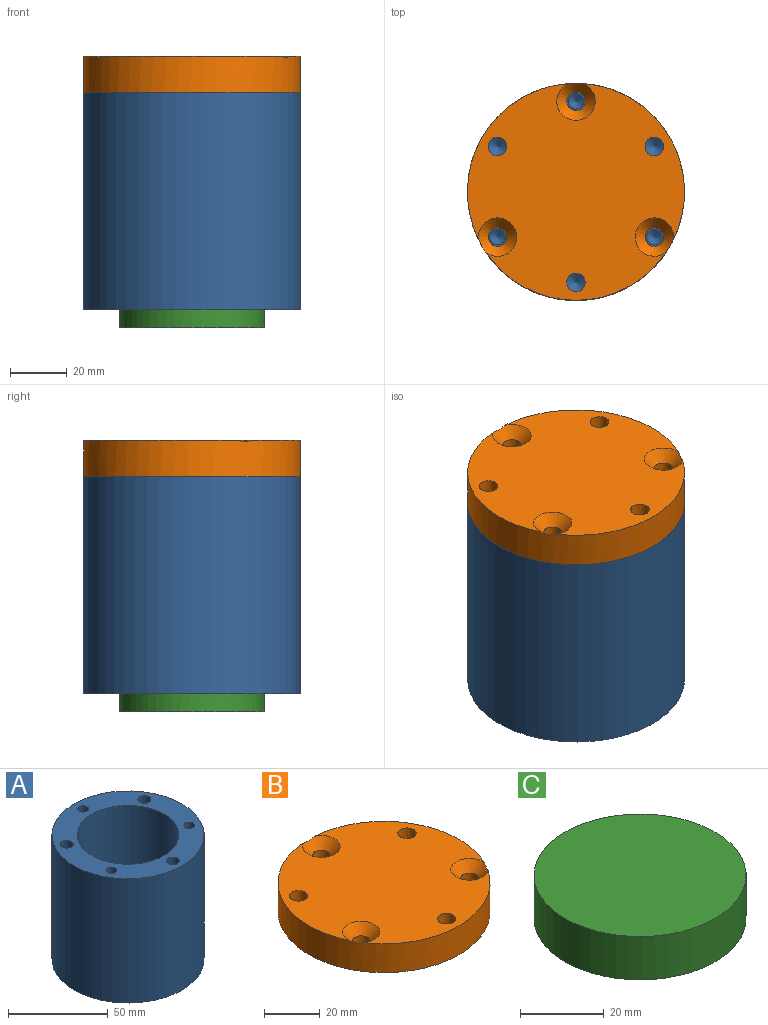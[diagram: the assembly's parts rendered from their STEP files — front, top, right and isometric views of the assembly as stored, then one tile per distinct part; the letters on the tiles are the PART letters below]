
ASSEMBLY  parts=3 mates=3
PART A: 16 faces, bbox 76.2x76.2x76.2 mm
  f0: cylinder r=25.5mm len=76.2mm, axis (0,0,-1), area 12208.9mm2, adj f2,f3
  f1: cylinder r=38.1mm len=76.2mm, axis (0,0,-1), area 18241.5mm2, adj f2,f3
  f2: plane 76.2x76.2mm, normal (0,0,1), area 2348.2mm2, adj f0,f1,f5,f7,f9,f11,f13,f15
  f3: plane 76.2x76.2mm, normal (0,0,-1), area 2517.5mm2, adj f0,f1
  f4: cone r=0mm half-angle=59deg, axis (0,0,1), area 26.8mm2, adj f5
  f5: cylinder r=2.71mm len=15.42mm, axis (0,0,1), area 262.1mm2, adj f2,f4
  f6: cone r=0mm half-angle=59deg, axis (0,0,1), area 26.8mm2, adj f7
  f7: cylinder r=2.71mm len=15.42mm, axis (0,0,1), area 262.1mm2, adj f2,f6
  f8: cone r=0mm half-angle=59deg, axis (0,0,1), area 26.8mm2, adj f9
  f9: cylinder r=2.71mm len=15.42mm, axis (0,0,1), area 262.1mm2, adj f2,f8
  f10: cone r=0mm half-angle=59deg, axis (0,0,1), area 39mm2, adj f11
  f11: cylinder r=3.26mm len=14.2mm, axis (0,0,1), area 291.2mm2, adj f2,f10
  f12: cone r=0mm half-angle=59deg, axis (0,0,1), area 39mm2, adj f13
  f13: cylinder r=3.26mm len=14.2mm, axis (0,0,1), area 291.2mm2, adj f2,f12
  f14: cone r=0mm half-angle=59deg, axis (0,0,1), area 39mm2, adj f15
  f15: cylinder r=3.26mm len=14.2mm, axis (0,0,1), area 291.2mm2, adj f2,f14
PART B: 12 faces, bbox 76.2x76.6x12.7 mm
  f0: cylinder r=38.1mm len=76.2mm, axis (0,0,-1), area 3034.9mm2, adj f1,f2,f3,f5,f7
  f1: plane 76.2x76.11mm, normal (0,0,1), area 4036.1mm2, adj f0,f3,f5,f7,f9,f10,f11
  f2: plane 76.2x76.2mm, normal (0,0,-1), area 4359.6mm2, adj f0,f4,f6,f8,f9,f10,f11
  f3: cone r=3.26mm half-angle=41deg, axis (0,0,1), area 164.4mm2, adj f0,f1,f4
  f4: cylinder r=3.26mm len=8.7mm, axis (0,0,1), area 178.4mm2, adj f2,f3
  f5: cone r=3.26mm half-angle=41deg, axis (0,0,1), area 164.4mm2, adj f0,f1,f6
  f6: cylinder r=3.26mm len=8.7mm, axis (0,0,1), area 178.4mm2, adj f2,f5
  f7: cone r=3.26mm half-angle=41deg, axis (0,0,1), area 164.4mm2, adj f0,f1,f8
  f8: cylinder r=3.26mm len=8.7mm, axis (0,0,1), area 178.4mm2, adj f2,f7
  f9: cylinder r=3.26mm len=12.7mm, axis (0,0,1), area 260.4mm2, adj f1,f2
  f10: cylinder r=3.26mm len=12.7mm, axis (0,0,1), area 260.4mm2, adj f1,f2
  f11: cylinder r=3.26mm len=12.7mm, axis (0,0,1), area 260.4mm2, adj f1,f2
PART C: 5 faces, bbox 50.8x50.8x12.7 mm
  f0: cylinder r=25.39mm len=50.77mm, axis (0,0,-1), area 2025.8mm2, adj f1,f2
  f1: plane 50.77x50.77mm, normal (0,0,1), area 2024.8mm2, adj f0
  f2: plane 50.77x50.77mm, normal (0,0,-1), area 2001.8mm2, adj f0,f4
  f3: cone r=0mm half-angle=59deg, axis (0,0,-1), area 26.8mm2, adj f4
  f4: cylinder r=2.71mm len=9.39mm, axis (0,0,-1), area 159.6mm2, adj f2,f3
PLACE A at identity fixed
PLACE B t=(0,0,76.2)mm
PLACE C rot(axis=(0,0,-1),90deg) t=(0,0,-6.35)mm
MATE cylindrical A.f1 <-> B.f0  axis (0,0,-1) through (0,0,38.1)mm
MATE planar A.f1 <-> B.f0  axis (0,0,1) through (0,0,76.2)mm
MATE cylindrical C.f0 <-> A.f0  axis (0,0,-1) through (0,0,0)mm
